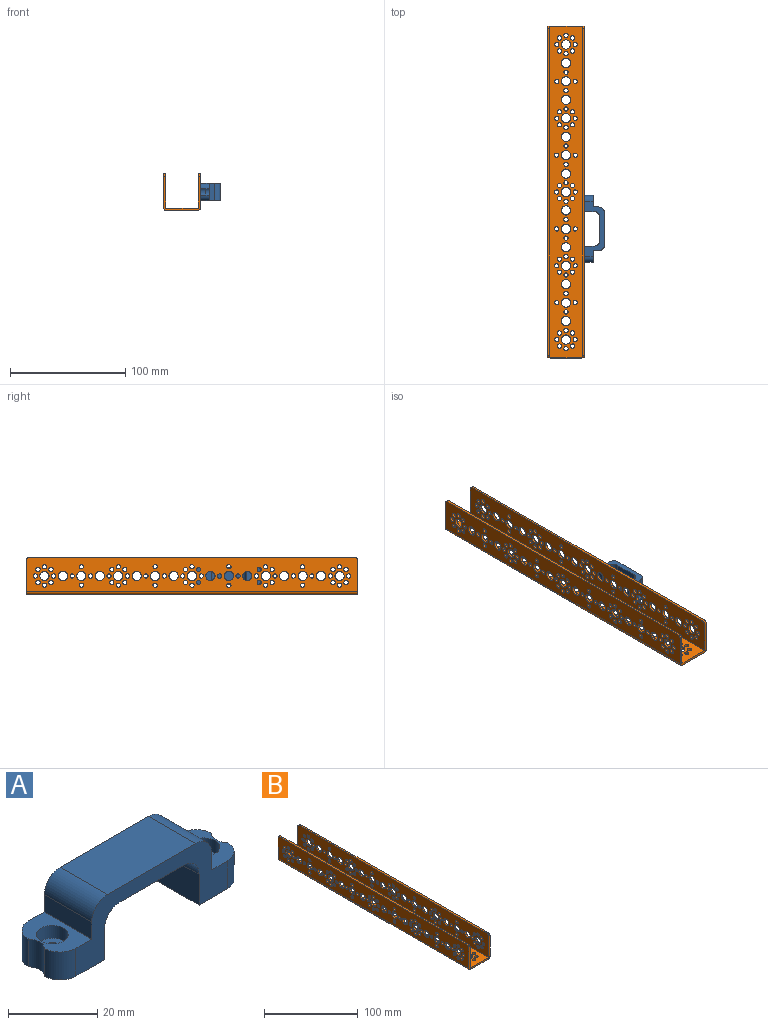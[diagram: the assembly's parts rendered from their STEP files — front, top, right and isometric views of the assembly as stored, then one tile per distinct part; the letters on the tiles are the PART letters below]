
ASSEMBLY  parts=2 mates=1
PART A: 28 faces, bbox 58x15x17.4 mm
  f0: cylinder r=5mm len=7.64mm, axis (0,0,1), area 58.6mm2, adj f6,f7,f8,f27
  f1: cylinder r=5mm len=7.64mm, axis (0,0,-1), area 59mm2, adj f4,f6,f12,f26
  f2: cylinder r=5mm len=7.64mm, axis (0,0,-1), area 58.7mm2, adj f5,f7,f8,f27
  f3: cylinder r=5mm len=7.64mm, axis (0,0,1), area 59.1mm2, adj f4,f5,f12,f26
  f4: plane 15x14mm, normal (0,0,-1), area 184.4mm2, adj f1,f3,f5,f6,f13,f16,f26
  f5: plane 48x17.36mm, normal (0,-1,0), area 335.3mm2, adj f2,f3,f4,f7,f8,f9,f10,f11
  f6: plane 48x17.36mm, normal (0,1,0), area 335.3mm2, adj f0,f1,f4,f7,f8,f9,f10,f11
  f7: plane 15x14mm, normal (0,0,-1), area 184.2mm2, adj f0,f2,f5,f6,f14,f19,f27
  f8: plane 15x10mm, normal (0,0,1), area 95.4mm2, adj f0,f2,f5,f6,f9,f21,f27
  f9: plane 15x4.72mm, normal (1,0,0), area 70.8mm2, adj f5,f6,f8,f24
  f10: plane 28x15mm, normal (0,0,1), area 420mm2, adj f5,f6,f24,f25
  f11: plane 15x4.72mm, normal (-1,0,0), area 70.8mm2, adj f5,f6,f12,f25
  f12: plane 15x10mm, normal (0,0,1), area 95.7mm2, adj f1,f3,f5,f6,f11,f18,f26
  f13: plane 15x8.36mm, normal (1,0,0), area 125.4mm2, adj f4,f5,f6,f23
  f14: plane 15x8.36mm, normal (-1,0,0), area 125.4mm2, adj f5,f6,f7,f22
  f15: plane 20x15mm, normal (0,0,-1), area 300mm2, adj f5,f6,f22,f23
  f16: cylinder r=1.9mm len=4.13mm, axis (0,0,1), area 49.3mm2, adj f4,f17
  f17: plane 7.14x7.14mm, normal (0,0,1), area 28.8mm2, adj f16,f18
  f18: cylinder r=3.57mm len=7.14mm, axis (0,0,1), area 78.7mm2, adj f12,f17
  f19: cylinder r=1.9mm len=4.13mm, axis (0,0,1), area 49.3mm2, adj f7,f20
  f20: plane 7.14x7.14mm, normal (0,0,1), area 28.8mm2, adj f19,f21
  f21: cylinder r=3.57mm len=7.14mm, axis (0,0,1), area 78.7mm2, adj f8,f20
  f22: cylinder r=5mm len=15mm, axis (0,-1,0), area 117.8mm2, adj f5,f6,f14,f15
  f23: cylinder r=5mm len=15mm, axis (0,1,0), area 117.8mm2, adj f5,f6,f13,f15
  f24: cylinder r=5mm len=15mm, axis (0,1,0), area 117.8mm2, adj f5,f6,f9,f10
  f25: cylinder r=5mm len=15mm, axis (0,1,0), area 117.8mm2, adj f5,f6,f10,f11
  f26: cylinder r=4mm len=7.64mm, axis (0,0,-1), area 43.6mm2, adj f1,f3,f4,f12
  f27: cylinder r=4mm len=7.64mm, axis (0,0,-1), area 44.7mm2, adj f0,f2,f7,f8
PART B: 235 faces, bbox 32x288x32 mm
  f0: plane 283x2mm, normal (0,0,1), area 566mm2, adj f1,f224,f225,f226
  f1: cylinder r=2.5mm len=2.5mm, axis (1,0,0), area 7.9mm2, adj f0,f223,f224,f226
  f2: cylinder r=4mm len=8mm, axis (1,0,0), area 50.3mm2, adj f224,f226
  f3: cylinder r=1.85mm len=3.7mm, axis (1,0,0), area 23.2mm2, adj f224,f226
  f4: cylinder r=1.85mm len=3.7mm, axis (1,0,0), area 23.2mm2, adj f224,f226
  f5: cylinder r=1.85mm len=3.7mm, axis (1,0,0), area 23.2mm2, adj f224,f226
  f6: cylinder r=1.85mm len=3.7mm, axis (1,0,0), area 23.2mm2, adj f224,f226
  f7: cylinder r=1.85mm len=3.7mm, axis (1,0,0), area 23.2mm2, adj f224,f226
  f8: cylinder r=1.85mm len=3.7mm, axis (1,0,0), area 23.2mm2, adj f224,f226
  f9: cylinder r=1.85mm len=3.7mm, axis (1,0,0), area 23.2mm2, adj f224,f226
  f10: cylinder r=1.85mm len=3.7mm, axis (1,0,0), area 23.2mm2, adj f224,f226
  f11: cylinder r=4mm len=8mm, axis (1,0,0), area 50.3mm2, adj f224,f226
  f12: cylinder r=1.85mm len=3.7mm, axis (1,0,0), area 23.2mm2, adj f224,f226
  f13: cylinder r=1.85mm len=3.7mm, axis (1,0,0), area 23.2mm2, adj f224,f226
  f14: cylinder r=1.85mm len=3.7mm, axis (1,0,0), area 23.2mm2, adj f224,f226
  f15: cylinder r=1.85mm len=3.7mm, axis (1,0,0), area 23.2mm2, adj f224,f226
  f16: cylinder r=1.85mm len=3.7mm, axis (1,0,0), area 23.2mm2, adj f224,f226
  f17: cylinder r=1.85mm len=3.7mm, axis (1,0,0), area 23.2mm2, adj f224,f226
  f18: cylinder r=1.85mm len=3.7mm, axis (1,0,0), area 23.2mm2, adj f224,f226
  f19: cylinder r=1.85mm len=3.7mm, axis (1,0,0), area 23.2mm2, adj f224,f226
  f20: cylinder r=4mm len=8mm, axis (1,0,0), area 50.3mm2, adj f224,f226
  f21: cylinder r=1.85mm len=3.7mm, axis (1,0,0), area 23.2mm2, adj f224,f226
  f22: cylinder r=1.85mm len=3.7mm, axis (1,0,0), area 23.2mm2, adj f224,f226
  f23: cylinder r=1.85mm len=3.7mm, axis (1,0,0), area 23.2mm2, adj f224,f226
  f24: cylinder r=1.85mm len=3.7mm, axis (1,0,0), area 23.2mm2, adj f224,f226
  f25: cylinder r=1.85mm len=3.7mm, axis (1,0,0), area 23.2mm2, adj f224,f226
  f26: cylinder r=1.85mm len=3.7mm, axis (1,0,0), area 23.2mm2, adj f224,f226
  f27: cylinder r=1.85mm len=3.7mm, axis (1,0,0), area 23.2mm2, adj f224,f226
  f28: cylinder r=1.85mm len=3.7mm, axis (1,0,0), area 23.2mm2, adj f224,f226
  f29: cylinder r=4mm len=8mm, axis (1,0,0), area 50.3mm2, adj f224,f226
  f30: cylinder r=1.85mm len=3.7mm, axis (1,0,0), area 23.2mm2, adj f224,f226
  f31: cylinder r=1.85mm len=3.7mm, axis (1,0,0), area 23.2mm2, adj f224,f226
  f32: cylinder r=1.85mm len=3.7mm, axis (1,0,0), area 23.2mm2, adj f224,f226
  f33: cylinder r=1.85mm len=3.7mm, axis (1,0,0), area 23.2mm2, adj f224,f226
  f34: cylinder r=1.85mm len=3.7mm, axis (1,0,0), area 23.2mm2, adj f224,f226
  f35: cylinder r=1.85mm len=3.7mm, axis (1,0,0), area 23.2mm2, adj f224,f226
  f36: cylinder r=1.85mm len=3.7mm, axis (1,0,0), area 23.2mm2, adj f224,f226
  f37: cylinder r=1.85mm len=3.7mm, axis (1,0,0), area 23.2mm2, adj f224,f226
  f38: cylinder r=4mm len=8mm, axis (1,0,0), area 50.3mm2, adj f224,f226
  f39: cylinder r=1.85mm len=3.7mm, axis (1,0,0), area 23.2mm2, adj f224,f226
  f40: cylinder r=1.85mm len=3.7mm, axis (1,0,0), area 23.2mm2, adj f224,f226
  f41: cylinder r=1.85mm len=3.7mm, axis (1,0,0), area 23.2mm2, adj f224,f226
  f42: cylinder r=1.85mm len=3.7mm, axis (1,0,0), area 23.2mm2, adj f224,f226
  f43: cylinder r=1.85mm len=3.7mm, axis (1,0,0), area 23.2mm2, adj f224,f226
  f44: cylinder r=1.85mm len=3.7mm, axis (1,0,0), area 23.2mm2, adj f224,f226
  f45: cylinder r=1.85mm len=3.7mm, axis (1,0,0), area 23.2mm2, adj f224,f226
  f46: cylinder r=1.85mm len=3.7mm, axis (1,0,0), area 23.2mm2, adj f224,f226
  f47: cylinder r=4mm len=8mm, axis (1,0,0), area 50.3mm2, adj f224,f226
  f48: cylinder r=1.85mm len=3.7mm, axis (1,0,0), area 23.2mm2, adj f224,f226
  f49: cylinder r=1.85mm len=3.7mm, axis (1,0,0), area 23.2mm2, adj f224,f226
  f50: cylinder r=1.85mm len=3.7mm, axis (1,0,0), area 23.2mm2, adj f224,f226
  f51: cylinder r=1.85mm len=3.7mm, axis (1,0,0), area 23.2mm2, adj f224,f226
  f52: cylinder r=4mm len=8mm, axis (1,0,0), area 50.3mm2, adj f224,f226
  f53: cylinder r=1.85mm len=3.7mm, axis (1,0,0), area 23.2mm2, adj f224,f226
  f54: cylinder r=1.85mm len=3.7mm, axis (1,0,0), area 23.2mm2, adj f224,f226
  f55: cylinder r=1.85mm len=3.7mm, axis (1,0,0), area 23.2mm2, adj f224,f226
  f56: cylinder r=1.85mm len=3.7mm, axis (1,0,0), area 23.2mm2, adj f224,f226
  f57: cylinder r=4mm len=8mm, axis (1,0,0), area 50.3mm2, adj f224,f226
  f58: cylinder r=1.85mm len=3.7mm, axis (1,0,0), area 23.2mm2, adj f224,f226
  f59: cylinder r=1.85mm len=3.7mm, axis (1,0,0), area 23.2mm2, adj f224,f226
  f60: cylinder r=1.85mm len=3.7mm, axis (1,0,0), area 23.2mm2, adj f224,f226
  f61: cylinder r=1.85mm len=3.7mm, axis (1,0,0), area 23.2mm2, adj f224,f226
  f62: cylinder r=4mm len=8mm, axis (1,0,0), area 50.3mm2, adj f224,f226
  f63: cylinder r=1.85mm len=3.7mm, axis (1,0,0), area 23.2mm2, adj f224,f226
  f64: cylinder r=1.85mm len=3.7mm, axis (1,0,0), area 23.2mm2, adj f224,f226
  f65: cylinder r=1.85mm len=3.7mm, axis (1,0,0), area 23.2mm2, adj f224,f226
  f66: cylinder r=1.85mm len=3.7mm, axis (1,0,0), area 23.2mm2, adj f224,f226
  f67: cylinder r=4mm len=8mm, axis (1,0,0), area 50.3mm2, adj f224,f226
  f68: cylinder r=4mm len=8mm, axis (1,0,0), area 50.3mm2, adj f224,f226
  f69: cylinder r=4mm len=8mm, axis (1,0,0), area 50.3mm2, adj f224,f226
  f70: cylinder r=4mm len=8mm, axis (1,0,0), area 50.3mm2, adj f224,f226
  f71: cylinder r=4mm len=8mm, axis (1,0,0), area 50.3mm2, adj f224,f226
  f72: cylinder r=4mm len=8mm, axis (1,0,0), area 50.3mm2, adj f224,f226
  f73: cylinder r=4mm len=8mm, axis (1,0,0), area 50.3mm2, adj f224,f226
  f74: cylinder r=4mm len=8mm, axis (1,0,0), area 50.3mm2, adj f224,f226
  f75: plane 283x2mm, normal (0,0,1), area 566mm2, adj f76,f228,f229,f230
  f76: cylinder r=2.5mm len=2.5mm, axis (1,0,0), area 7.9mm2, adj f75,f223,f228,f230
  f77: cylinder r=4mm len=8mm, axis (1,0,0), area 50.3mm2, adj f228,f230
  f78: cylinder r=1.85mm len=3.7mm, axis (1,0,0), area 23.2mm2, adj f228,f230
  f79: cylinder r=1.85mm len=3.7mm, axis (1,0,0), area 23.2mm2, adj f228,f230
  f80: cylinder r=1.85mm len=3.7mm, axis (1,0,0), area 23.2mm2, adj f228,f230
  f81: cylinder r=1.85mm len=3.7mm, axis (1,0,0), area 23.2mm2, adj f228,f230
  f82: cylinder r=1.85mm len=3.7mm, axis (1,0,0), area 23.2mm2, adj f228,f230
  f83: cylinder r=1.85mm len=3.7mm, axis (1,0,0), area 23.2mm2, adj f228,f230
  f84: cylinder r=1.85mm len=3.7mm, axis (1,0,0), area 23.2mm2, adj f228,f230
  f85: cylinder r=1.85mm len=3.7mm, axis (1,0,0), area 23.2mm2, adj f228,f230
  f86: cylinder r=4mm len=8mm, axis (1,0,0), area 50.3mm2, adj f228,f230
  f87: cylinder r=1.85mm len=3.7mm, axis (1,0,0), area 23.2mm2, adj f228,f230
  f88: cylinder r=1.85mm len=3.7mm, axis (1,0,0), area 23.2mm2, adj f228,f230
  f89: cylinder r=1.85mm len=3.7mm, axis (1,0,0), area 23.2mm2, adj f228,f230
  f90: cylinder r=1.85mm len=3.7mm, axis (1,0,0), area 23.2mm2, adj f228,f230
  f91: cylinder r=1.85mm len=3.7mm, axis (1,0,0), area 23.2mm2, adj f228,f230
  f92: cylinder r=1.85mm len=3.7mm, axis (1,0,0), area 23.2mm2, adj f228,f230
  f93: cylinder r=1.85mm len=3.7mm, axis (1,0,0), area 23.2mm2, adj f228,f230
  f94: cylinder r=1.85mm len=3.7mm, axis (1,0,0), area 23.2mm2, adj f228,f230
  f95: cylinder r=4mm len=8mm, axis (1,0,0), area 50.3mm2, adj f228,f230
  f96: cylinder r=1.85mm len=3.7mm, axis (1,0,0), area 23.2mm2, adj f228,f230
  f97: cylinder r=1.85mm len=3.7mm, axis (1,0,0), area 23.2mm2, adj f228,f230
  f98: cylinder r=1.85mm len=3.7mm, axis (1,0,0), area 23.2mm2, adj f228,f230
  f99: cylinder r=1.85mm len=3.7mm, axis (1,0,0), area 23.2mm2, adj f228,f230
  f100: cylinder r=1.85mm len=3.7mm, axis (1,0,0), area 23.2mm2, adj f228,f230
  f101: cylinder r=1.85mm len=3.7mm, axis (1,0,0), area 23.2mm2, adj f228,f230
  f102: cylinder r=1.85mm len=3.7mm, axis (1,0,0), area 23.2mm2, adj f228,f230
  f103: cylinder r=1.85mm len=3.7mm, axis (1,0,0), area 23.2mm2, adj f228,f230
  f104: cylinder r=4mm len=8mm, axis (1,0,0), area 50.3mm2, adj f228,f230
  f105: cylinder r=1.85mm len=3.7mm, axis (1,0,0), area 23.2mm2, adj f228,f230
  f106: cylinder r=1.85mm len=3.7mm, axis (1,0,0), area 23.2mm2, adj f228,f230
  f107: cylinder r=1.85mm len=3.7mm, axis (1,0,0), area 23.2mm2, adj f228,f230
  f108: cylinder r=1.85mm len=3.7mm, axis (1,0,0), area 23.2mm2, adj f228,f230
  f109: cylinder r=1.85mm len=3.7mm, axis (1,0,0), area 23.2mm2, adj f228,f230
  f110: cylinder r=1.85mm len=3.7mm, axis (1,0,0), area 23.2mm2, adj f228,f230
  f111: cylinder r=1.85mm len=3.7mm, axis (1,0,0), area 23.2mm2, adj f228,f230
  f112: cylinder r=1.85mm len=3.7mm, axis (1,0,0), area 23.2mm2, adj f228,f230
  f113: cylinder r=4mm len=8mm, axis (1,0,0), area 50.3mm2, adj f228,f230
  f114: cylinder r=1.85mm len=3.7mm, axis (1,0,0), area 23.2mm2, adj f228,f230
  f115: cylinder r=1.85mm len=3.7mm, axis (1,0,0), area 23.2mm2, adj f228,f230
  f116: cylinder r=1.85mm len=3.7mm, axis (1,0,0), area 23.2mm2, adj f228,f230
  f117: cylinder r=1.85mm len=3.7mm, axis (1,0,0), area 23.2mm2, adj f228,f230
  f118: cylinder r=1.85mm len=3.7mm, axis (1,0,0), area 23.2mm2, adj f228,f230
  f119: cylinder r=1.85mm len=3.7mm, axis (1,0,0), area 23.2mm2, adj f228,f230
  f120: cylinder r=1.85mm len=3.7mm, axis (1,0,0), area 23.2mm2, adj f228,f230
  f121: cylinder r=1.85mm len=3.7mm, axis (1,0,0), area 23.2mm2, adj f228,f230
  f122: cylinder r=4mm len=8mm, axis (1,0,0), area 50.3mm2, adj f228,f230
  f123: cylinder r=1.85mm len=3.7mm, axis (1,0,0), area 23.2mm2, adj f228,f230
  f124: cylinder r=1.85mm len=3.7mm, axis (1,0,0), area 23.2mm2, adj f228,f230
  f125: cylinder r=1.85mm len=3.7mm, axis (1,0,0), area 23.2mm2, adj f228,f230
  f126: cylinder r=1.85mm len=3.7mm, axis (1,0,0), area 23.2mm2, adj f228,f230
  f127: cylinder r=4mm len=8mm, axis (1,0,0), area 50.3mm2, adj f228,f230
  f128: cylinder r=1.85mm len=3.7mm, axis (1,0,0), area 23.2mm2, adj f228,f230
  f129: cylinder r=1.85mm len=3.7mm, axis (1,0,0), area 23.2mm2, adj f228,f230
  f130: cylinder r=1.85mm len=3.7mm, axis (1,0,0), area 23.2mm2, adj f228,f230
  f131: cylinder r=1.85mm len=3.7mm, axis (1,0,0), area 23.2mm2, adj f228,f230
  f132: cylinder r=4mm len=8mm, axis (1,0,0), area 50.3mm2, adj f228,f230
  f133: cylinder r=1.85mm len=3.7mm, axis (1,0,0), area 23.2mm2, adj f228,f230
  f134: cylinder r=1.85mm len=3.7mm, axis (1,0,0), area 23.2mm2, adj f228,f230
  f135: cylinder r=1.85mm len=3.7mm, axis (1,0,0), area 23.2mm2, adj f228,f230
  f136: cylinder r=1.85mm len=3.7mm, axis (1,0,0), area 23.2mm2, adj f228,f230
  f137: cylinder r=4mm len=8mm, axis (1,0,0), area 50.3mm2, adj f228,f230
  f138: cylinder r=1.85mm len=3.7mm, axis (1,0,0), area 23.2mm2, adj f228,f230
  f139: cylinder r=1.85mm len=3.7mm, axis (1,0,0), area 23.2mm2, adj f228,f230
  f140: cylinder r=1.85mm len=3.7mm, axis (1,0,0), area 23.2mm2, adj f228,f230
  f141: cylinder r=1.85mm len=3.7mm, axis (1,0,0), area 23.2mm2, adj f228,f230
  f142: cylinder r=4mm len=8mm, axis (1,0,0), area 50.3mm2, adj f228,f230
  f143: cylinder r=4mm len=8mm, axis (1,0,0), area 50.3mm2, adj f228,f230
  f144: cylinder r=4mm len=8mm, axis (1,0,0), area 50.3mm2, adj f228,f230
  f145: cylinder r=4mm len=8mm, axis (1,0,0), area 50.3mm2, adj f228,f230
  f146: cylinder r=4mm len=8mm, axis (1,0,0), area 50.3mm2, adj f228,f230
  f147: cylinder r=4mm len=8mm, axis (1,0,0), area 50.3mm2, adj f228,f230
  f148: cylinder r=4mm len=8mm, axis (1,0,0), area 50.3mm2, adj f228,f230
  f149: cylinder r=4mm len=8mm, axis (1,0,0), area 50.3mm2, adj f228,f230
  f150: cylinder r=4mm len=8mm, axis (0,0,1), area 50.3mm2, adj f227,f232
  f151: cylinder r=1.85mm len=3.7mm, axis (0,0,1), area 23.2mm2, adj f227,f232
  f152: cylinder r=1.85mm len=3.7mm, axis (0,0,1), area 23.2mm2, adj f227,f232
  f153: cylinder r=1.85mm len=3.7mm, axis (0,0,1), area 23.2mm2, adj f227,f232
  f154: cylinder r=1.85mm len=3.7mm, axis (0,0,1), area 23.2mm2, adj f227,f232
  f155: cylinder r=1.85mm len=3.7mm, axis (0,0,1), area 23.2mm2, adj f227,f232
  f156: cylinder r=1.85mm len=3.7mm, axis (0,0,1), area 23.2mm2, adj f227,f232
  f157: cylinder r=1.85mm len=3.7mm, axis (0,0,1), area 23.2mm2, adj f227,f232
  f158: cylinder r=1.85mm len=3.7mm, axis (0,0,1), area 23.2mm2, adj f227,f232
  f159: cylinder r=4mm len=8mm, axis (0,0,1), area 50.3mm2, adj f227,f232
  f160: cylinder r=1.85mm len=3.7mm, axis (0,0,1), area 23.2mm2, adj f227,f232
  f161: cylinder r=1.85mm len=3.7mm, axis (0,0,1), area 23.2mm2, adj f227,f232
  f162: cylinder r=1.85mm len=3.7mm, axis (0,0,1), area 23.2mm2, adj f227,f232
  f163: cylinder r=1.85mm len=3.7mm, axis (0,0,1), area 23.2mm2, adj f227,f232
  f164: cylinder r=1.85mm len=3.7mm, axis (0,0,1), area 23.2mm2, adj f227,f232
  f165: cylinder r=1.85mm len=3.7mm, axis (0,0,1), area 23.2mm2, adj f227,f232
  f166: cylinder r=1.85mm len=3.7mm, axis (0,0,1), area 23.2mm2, adj f227,f232
  f167: cylinder r=1.85mm len=3.7mm, axis (0,0,1), area 23.2mm2, adj f227,f232
  f168: cylinder r=4mm len=8mm, axis (0,0,1), area 50.3mm2, adj f227,f232
  f169: cylinder r=1.85mm len=3.7mm, axis (0,0,1), area 23.2mm2, adj f227,f232
  f170: cylinder r=1.85mm len=3.7mm, axis (0,0,1), area 23.2mm2, adj f227,f232
  f171: cylinder r=1.85mm len=3.7mm, axis (0,0,1), area 23.2mm2, adj f227,f232
  f172: cylinder r=1.85mm len=3.7mm, axis (0,0,1), area 23.2mm2, adj f227,f232
  f173: cylinder r=1.85mm len=3.7mm, axis (0,0,1), area 23.2mm2, adj f227,f232
  f174: cylinder r=1.85mm len=3.7mm, axis (0,0,1), area 23.2mm2, adj f227,f232
  f175: cylinder r=1.85mm len=3.7mm, axis (0,0,1), area 23.2mm2, adj f227,f232
  f176: cylinder r=1.85mm len=3.7mm, axis (0,0,1), area 23.2mm2, adj f227,f232
  f177: cylinder r=4mm len=8mm, axis (0,0,1), area 50.3mm2, adj f227,f232
  f178: cylinder r=1.85mm len=3.7mm, axis (0,0,1), area 23.2mm2, adj f227,f232
  f179: cylinder r=1.85mm len=3.7mm, axis (0,0,1), area 23.2mm2, adj f227,f232
  f180: cylinder r=1.85mm len=3.7mm, axis (0,0,1), area 23.2mm2, adj f227,f232
  f181: cylinder r=1.85mm len=3.7mm, axis (0,0,1), area 23.2mm2, adj f227,f232
  f182: cylinder r=1.85mm len=3.7mm, axis (0,0,1), area 23.2mm2, adj f227,f232
  f183: cylinder r=1.85mm len=3.7mm, axis (0,0,1), area 23.2mm2, adj f227,f232
  f184: cylinder r=1.85mm len=3.7mm, axis (0,0,1), area 23.2mm2, adj f227,f232
  f185: cylinder r=1.85mm len=3.7mm, axis (0,0,1), area 23.2mm2, adj f227,f232
  f186: cylinder r=4mm len=8mm, axis (0,0,1), area 50.3mm2, adj f227,f232
  f187: cylinder r=1.85mm len=3.7mm, axis (0,0,1), area 23.2mm2, adj f227,f232
  f188: cylinder r=1.85mm len=3.7mm, axis (0,0,1), area 23.2mm2, adj f227,f232
  f189: cylinder r=1.85mm len=3.7mm, axis (0,0,1), area 23.2mm2, adj f227,f232
  f190: cylinder r=1.85mm len=3.7mm, axis (0,0,1), area 23.2mm2, adj f227,f232
  f191: cylinder r=1.85mm len=3.7mm, axis (0,0,1), area 23.2mm2, adj f227,f232
  f192: cylinder r=1.85mm len=3.7mm, axis (0,0,1), area 23.2mm2, adj f227,f232
  f193: cylinder r=1.85mm len=3.7mm, axis (0,0,1), area 23.2mm2, adj f227,f232
  f194: cylinder r=1.85mm len=3.7mm, axis (0,0,1), area 23.2mm2, adj f227,f232
  f195: cylinder r=4mm len=8mm, axis (0,0,1), area 50.3mm2, adj f227,f232
  f196: cylinder r=1.85mm len=3.7mm, axis (0,0,1), area 23.2mm2, adj f227,f232
  f197: cylinder r=1.85mm len=3.7mm, axis (0,0,1), area 23.2mm2, adj f227,f232
  f198: cylinder r=1.85mm len=3.7mm, axis (0,0,1), area 23.2mm2, adj f227,f232
  f199: cylinder r=1.85mm len=3.7mm, axis (0,0,1), area 23.2mm2, adj f227,f232
  f200: cylinder r=4mm len=8mm, axis (0,0,1), area 50.3mm2, adj f227,f232
  f201: cylinder r=1.85mm len=3.7mm, axis (0,0,1), area 23.2mm2, adj f227,f232
  f202: cylinder r=1.85mm len=3.7mm, axis (0,0,1), area 23.2mm2, adj f227,f232
  f203: cylinder r=1.85mm len=3.7mm, axis (0,0,1), area 23.2mm2, adj f227,f232
  f204: cylinder r=1.85mm len=3.7mm, axis (0,0,1), area 23.2mm2, adj f227,f232
  f205: cylinder r=4mm len=8mm, axis (0,0,1), area 50.3mm2, adj f227,f232
  f206: cylinder r=1.85mm len=3.7mm, axis (0,0,1), area 23.2mm2, adj f227,f232
  f207: cylinder r=1.85mm len=3.7mm, axis (0,0,1), area 23.2mm2, adj f227,f232
  f208: cylinder r=1.85mm len=3.7mm, axis (0,0,1), area 23.2mm2, adj f227,f232
  f209: cylinder r=1.85mm len=3.7mm, axis (0,0,1), area 23.2mm2, adj f227,f232
  f210: cylinder r=4mm len=8mm, axis (0,0,1), area 50.3mm2, adj f227,f232
  f211: cylinder r=1.85mm len=3.7mm, axis (0,0,1), area 23.2mm2, adj f227,f232
  f212: cylinder r=1.85mm len=3.7mm, axis (0,0,1), area 23.2mm2, adj f227,f232
  f213: cylinder r=1.85mm len=3.7mm, axis (0,0,1), area 23.2mm2, adj f227,f232
  f214: cylinder r=1.85mm len=3.7mm, axis (0,0,1), area 23.2mm2, adj f227,f232
  f215: cylinder r=4mm len=8mm, axis (0,0,1), area 50.3mm2, adj f227,f232
  f216: cylinder r=4mm len=8mm, axis (0,0,1), area 50.3mm2, adj f227,f232
  f217: cylinder r=4mm len=8mm, axis (0,0,1), area 50.3mm2, adj f227,f232
  f218: cylinder r=4mm len=8mm, axis (0,0,1), area 50.3mm2, adj f227,f232
  f219: cylinder r=4mm len=8mm, axis (0,0,1), area 50.3mm2, adj f227,f232
  f220: cylinder r=4mm len=8mm, axis (0,0,1), area 50.3mm2, adj f227,f232
  f221: cylinder r=4mm len=8mm, axis (0,0,1), area 50.3mm2, adj f227,f232
  f222: cylinder r=4mm len=8mm, axis (0,0,1), area 50.3mm2, adj f227,f232
  f223: plane 32.01x29.5mm, normal (0,1,0), area 171.3mm2, adj f1,f76,f224,f226,f227,f228,f230,f231
  f224: plane 288.01x29.5mm, normal (1,0,0), area 7036.6mm2, adj f0,f1,f2,f3,f4,f5,f6,f7
  f225: cylinder r=2.5mm len=2.5mm, axis (-1,0,0), area 7.9mm2, adj f0,f224,f226,f234
  f226: plane 288.01x30mm, normal (-1,0,0), area 7180.6mm2, adj f0,f1,f2,f3,f4,f5,f6,f7
  f227: plane 288x28mm, normal (0,0,1), area 6607.3mm2, adj f150,f151,f152,f153,f154,f155,f156,f157
  f228: plane 288.01x30mm, normal (1,0,0), area 7180.6mm2, adj f75,f76,f77,f78,f79,f80,f81,f82
  f229: cylinder r=2.5mm len=2.5mm, axis (-1,0,0), area 7.9mm2, adj f75,f228,f230,f234
  f230: plane 288.01x29.5mm, normal (-1,0,0), area 7036.6mm2, adj f75,f76,f77,f78,f79,f80,f81,f82
  f231: cylinder r=2.5mm len=288mm, axis (0,1,0), area 1131mm2, adj f223,f230,f232,f234
  f232: plane 288x27mm, normal (0,0,-1), area 6319.3mm2, adj f150,f151,f152,f153,f154,f155,f156,f157
  f233: cylinder r=2.5mm len=288mm, axis (0,1,0), area 1131mm2, adj f223,f224,f232,f234
  f234: plane 32.01x29.5mm, normal (0,-1,0), area 171.3mm2, adj f224,f225,f226,f227,f228,f229,f230,f231
PLACE A rot(axis=(-0.58,0.58,-0.58),120deg) t=(39.82,68.46,-0.18)mm
PLACE B rot(axis=(-0.21,-0.31,0.93),0deg) t=(23.82,-25.85,-8.68)mm
MATE fastened B.f14 <-> A.f19  axis (1,0,0) through (39.82,46.15,7.32)mm
